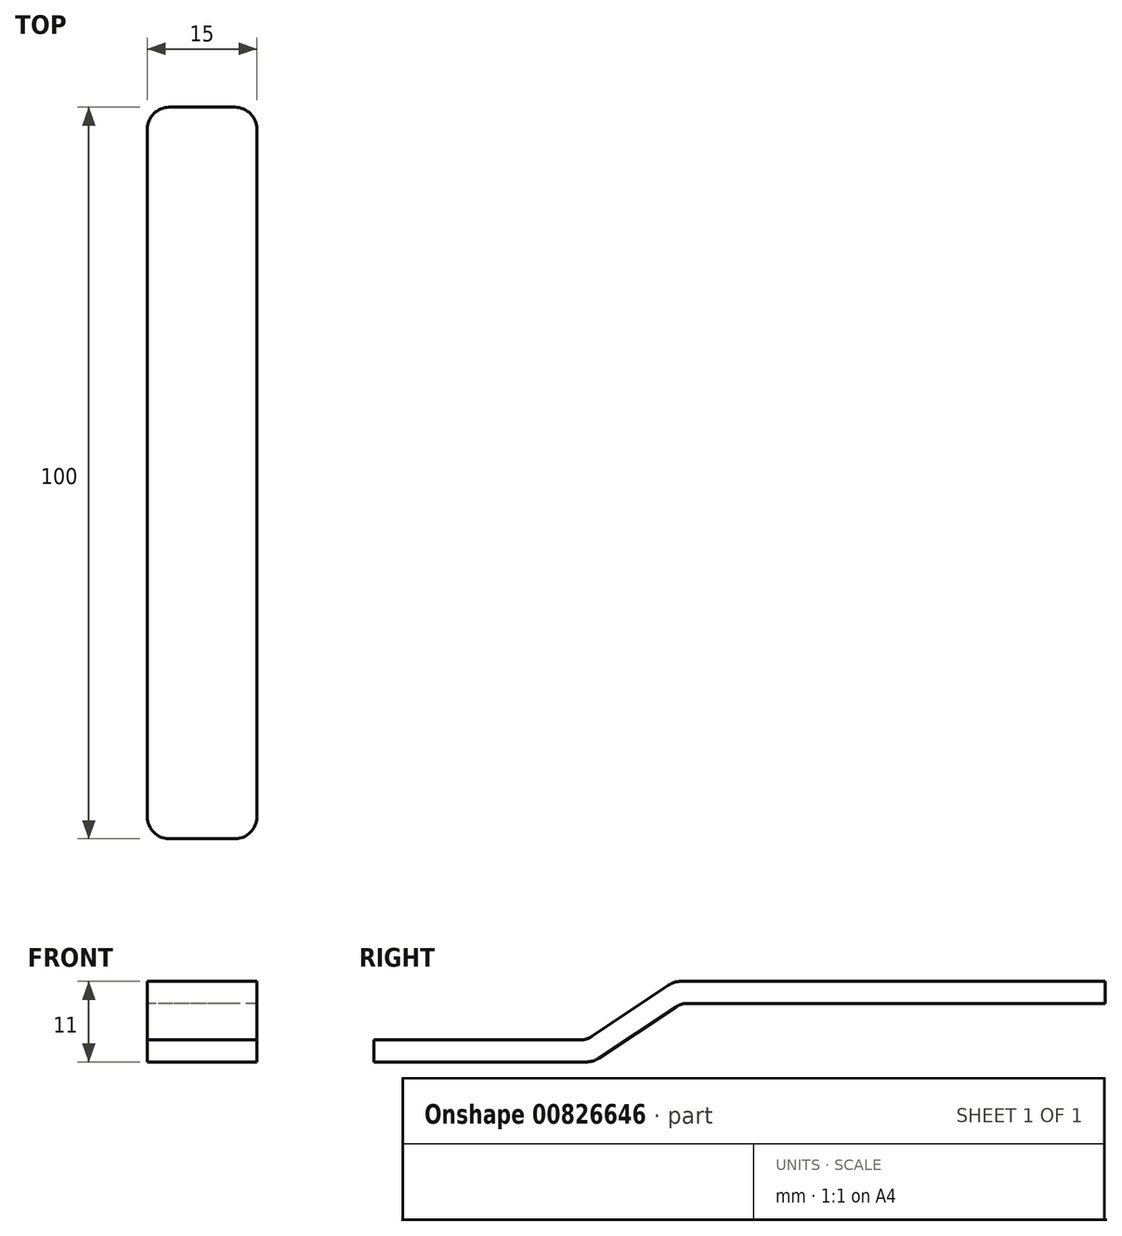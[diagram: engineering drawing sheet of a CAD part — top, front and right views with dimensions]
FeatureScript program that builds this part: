
annotation { "Feature Type Name" : "Feature", "Feature Type Description" : "" }
export const myFeature = defineFeature(function(context is Context, id is Id, definition is map)
    precondition{}
    {
        {
            var Q0;
            Q0=qCreatedBy(makeId("Right.planeOp"),FACE);
            var sketch = newSketch(context, id + "F0", { "sketchPlane" : qUnion([Q0])});
            skLineSegment(sketch, "E0", {"start": v(0, 0) * mm, "end": v(30, 0) * mm});
            skLineSegment(sketch, "E1", {"start": v(30, 0) * mm, "end": v(42, 8) * mm});
            skLineSegment(sketch, "E2", {"start": v(42, 8) * mm, "end": v(100, 8) * mm});
            skLineSegment(sketch, "E3", {"start": v(100, 8) * mm, "end": v(100, 11) * mm});
            skLineSegment(sketch, "E4", {"start": v(100, 11) * mm, "end": v(41.1, 11) * mm});
            skLineSegment(sketch, "E5", {"start": v(41.1, 11) * mm, "end": v(29.1, 3) * mm});
            skLineSegment(sketch, "E6", {"start": v(29.1, 3) * mm, "end": v(0, 3) * mm});
            skLineSegment(sketch, "E7", {"start": v(0, 3) * mm, "end": v(0, 0) * mm});
            skSolve(sketch);
        }
        {
            var Q0;
            Q0=makeQuery(id+"F0.imprint","IMPRINT",FACE,{"disambiguationData":[TD([[makeQuery(id+"F0.imprint","IMPRINT",EDGE,{"derivedFrom":sQuery(id+"F0.wireOp",EDGE,"E0")}),1.0]])]});
            extrude(context, id + "F1", {"entities" : qUnion([Q0]), "endBound" : BoundingType.SYMMETRIC, "depth" : 15 * mm, "offsetDistance" : 25.4 * mm});
        }
        {
            var Q0;
            Q0=makeQuery(id+"F1.opExtrude","CAP_EDGE",EDGE,{"disambiguationData":[OSD([sQuery(id+"F0.wireOp",EDGE,"E7")])],"isStart":false});
            var Q1;
            Q1=makeQuery(id+"F1.opExtrude","CAP_EDGE",EDGE,{"disambiguationData":[OSD([sQuery(id+"F0.wireOp",EDGE,"E7")])],"isStart":true});
            var Q2;
            Q2=makeQuery(id+"F1.opExtrude","SWEPT_EDGE",EDGE,{"disambiguationData":[OSD([sQuery(id+"F0.wireOp",EDGE,"E4"),sQuery(id+"F0.wireOp",EDGE,"E5")])]});
            var Q3;
            Q3=makeQuery(id+"F1.opExtrude","SWEPT_EDGE",EDGE,{"disambiguationData":[OSD([sQuery(id+"F0.wireOp",EDGE,"E5"),sQuery(id+"F0.wireOp",EDGE,"E6")])]});
            var Q4;
            Q4=makeQuery(id+"F1.opExtrude","SWEPT_EDGE",EDGE,{"disambiguationData":[OSD([sQuery(id+"F0.wireOp",EDGE,"E0"),sQuery(id+"F0.wireOp",EDGE,"E1")])]});
            var Q5;
            Q5=makeQuery(id+"F1.opExtrude","SWEPT_EDGE",EDGE,{"disambiguationData":[OSD([sQuery(id+"F0.wireOp",EDGE,"E1"),sQuery(id+"F0.wireOp",EDGE,"E2")])]});
            var Q6;
            Q6=makeQuery(id+"F1.opExtrude","CAP_EDGE",EDGE,{"disambiguationData":[OSD([sQuery(id+"F0.wireOp",EDGE,"E3")])],"isStart":false});
            var Q7;
            Q7=makeQuery(id+"F1.opExtrude","CAP_EDGE",EDGE,{"disambiguationData":[OSD([sQuery(id+"F0.wireOp",EDGE,"E3")])],"isStart":true});
            fillet(context, id + "F2", {"entities" : qUnion([Q0, Q1, Q2, Q3, Q4, Q5, Q6, Q7]), "radius" : 3 * mm, "tangentPropagation" : true, "allowEdgeOverflow" : false});
        }
    });
